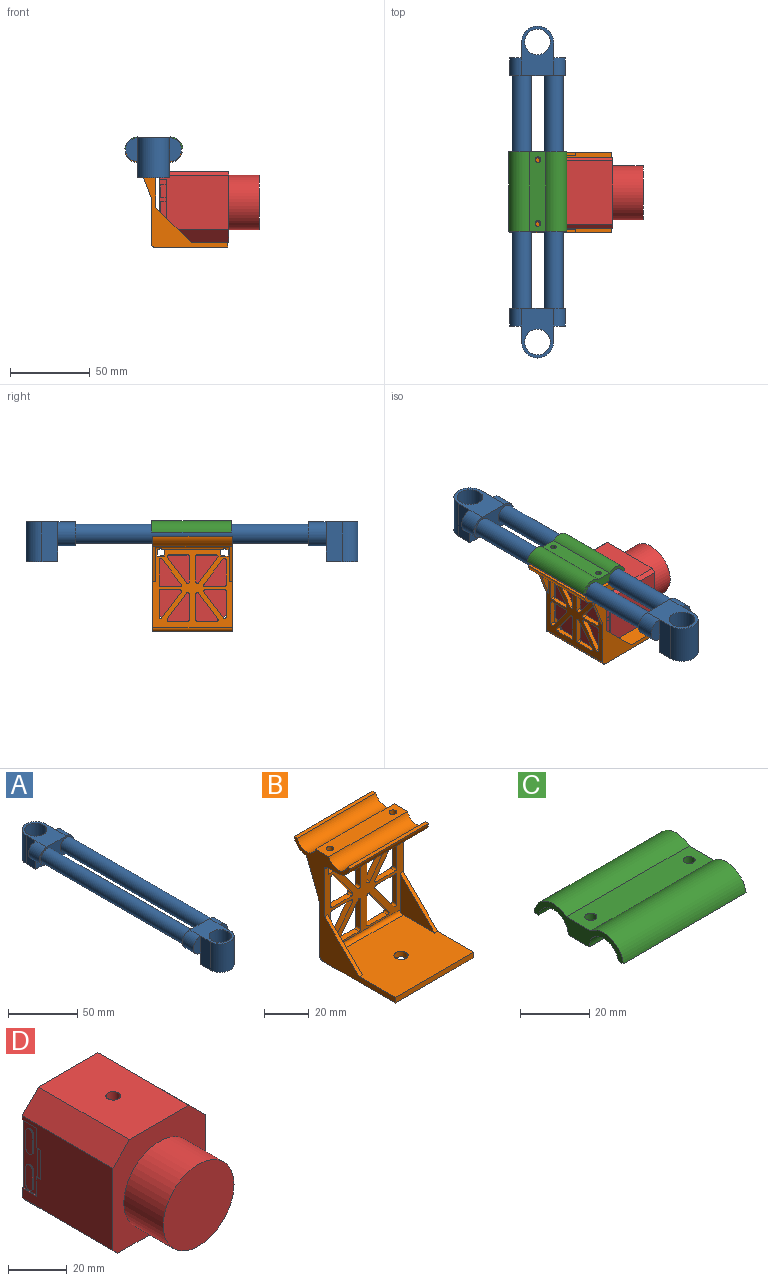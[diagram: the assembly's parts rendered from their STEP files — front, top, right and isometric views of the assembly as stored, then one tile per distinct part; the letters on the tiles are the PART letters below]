
ASSEMBLY  parts=4 mates=3
PART A: 28 faces, bbox 35x208x25 mm
  f0: plane 15x7.5mm, normal (0,1,0), area 88.4mm2, adj f11,f23
  f1: plane 15x7.5mm, normal (0,-1,0), area 88.4mm2, adj f7,f20
  f2: cylinder r=7.5mm len=15mm, axis (0,1,0), area 259.2mm2, adj f3,f4,f5,f6
  f3: plane 31x20mm, normal (0,0,1), area 376mm2, adj f2,f5,f7,f17,f18,f19,f20
  f4: plane 20x11mm, normal (0,0,-1), area 220mm2, adj f2,f5,f7,f16
  f5: plane 35x15mm, normal (0,1,0), area 250.5mm2, adj f2,f3,f4,f7,f8,f9
  f6: plane 15x7.5mm, normal (0,-1,0), area 88.4mm2, adj f2,f17
  f7: cylinder r=7.5mm len=15mm, axis (0,1,0), area 259.2mm2, adj f1,f3,f4,f5
  f8: cylinder r=6mm len=146mm, axis (0,1,0), area 5504.1mm2, adj f5,f10
  f9: cylinder r=6mm len=146mm, axis (0,1,0), area 5504.1mm2, adj f5,f10
  f10: plane 35x15mm, normal (0,-1,0), area 250.5mm2, adj f8,f9,f11,f12,f13,f14
  f11: cylinder r=7.5mm len=15mm, axis (0,-1,0), area 259.2mm2, adj f0,f10,f12,f13
  f12: plane 20x11mm, normal (0,0,-1), area 220mm2, adj f10,f11,f14,f22
  f13: plane 31x20mm, normal (0,0,1), area 376mm2, adj f10,f11,f14,f23,f24,f25,f26
  f14: cylinder r=7.5mm len=15mm, axis (0,-1,0), area 259.2mm2, adj f10,f12,f13,f15
  f15: plane 15x7.5mm, normal (0,1,0), area 88.4mm2, adj f14,f26
  f16: plane 20x10mm, normal (0,1,0), area 200mm2, adj f4,f17,f20,f21
  f17: plane 25x10mm, normal (-1,0,0), area 250mm2, adj f3,f6,f16,f18,f21
  f18: cylinder r=10mm len=25mm, axis (0,0,1), area 785.4mm2, adj f3,f17,f20,f21
  f19: cylinder r=8mm len=25mm, axis (0,0,1), area 1256.6mm2, adj f3,f21
  f20: plane 25x10mm, normal (1,0,0), area 250mm2, adj f1,f3,f16,f18,f21
  f21: plane 20x20mm, normal (0,0,-1), area 156mm2, adj f16,f17,f18,f19,f20
  f22: plane 20x10mm, normal (0,-1,0), area 200mm2, adj f12,f23,f26,f27
  f23: plane 25x10mm, normal (-1,0,0), area 250mm2, adj f0,f13,f22,f24,f27
  f24: cylinder r=10mm len=25mm, axis (0,0,1), area 785.4mm2, adj f13,f23,f26,f27
  f25: cylinder r=8mm len=25mm, axis (0,0,1), area 1256.6mm2, adj f13,f27
  f26: plane 25x10mm, normal (1,0,0), area 250mm2, adj f13,f15,f22,f24,f27
  f27: plane 20x20mm, normal (0,0,-1), area 156mm2, adj f22,f23,f24,f25,f26
PART B: 89 faces, bbox 50x64.4x59.5 mm
  f0: plane 50x46mm, normal (0,-1,0), area 1006.9mm2, adj f3,f6,f18,f19,f22,f23,f26,f27
  f1: plane 50x49mm, normal (0,1,0), area 1156.9mm2, adj f2,f13,f18,f19,f20,f21,f24,f25
  f2: cylinder r=2mm len=46mm, axis (-1,0,0), area 141.6mm2, adj f1,f7,f21,f25,f28,f29,f33,f34
  f3: cylinder r=2mm len=50mm, axis (-1,0,0), area 154.2mm2, adj f0,f10,f18,f19,f28,f29,f33,f34
  f4: plane 50x8.5mm, normal (0,0,1), area 405.8mm2, adj f16,f17,f18,f19,f28,f29
  f5: plane 50x43mm, normal (0,0,1), area 2038.3mm2, adj f6,f11,f18,f19,f22,f23,f26,f27
  f6: cylinder r=2mm len=46mm, axis (-1,0,0), area 144.5mm2, adj f0,f5,f23,f27
  f7: plane 46x6.5mm, normal (0,0,-1), area 299mm2, adj f2,f14,f21,f25
  f8: plane 50x2.05mm, normal (0,0,1), area 102.4mm2, adj f9,f17,f18,f19
  f9: cylinder r=8mm len=50mm, axis (-1,0,0), area 552.9mm2, adj f8,f10,f18,f19
  f10: plane 50x6.5mm, normal (0,0,-1), area 325mm2, adj f3,f9,f18,f19
  f11: plane 50x3mm, normal (0,-1,0), area 150mm2, adj f5,f12,f18,f19
  f12: plane 50x46mm, normal (0,0,-1), area 2268.3mm2, adj f11,f13,f18,f19,f40
  f13: cylinder r=2mm len=50mm, axis (-1,0,0), area 157.1mm2, adj f1,f12,f18,f19
  f14: cylinder r=8mm len=50mm, axis (-1,0,0), area 552.9mm2, adj f7,f15,f18,f19,f20,f24
  f15: plane 50x2.05mm, normal (0,0,1), area 102.4mm2, adj f14,f16,f18,f19
  f16: cylinder r=6mm len=50mm, axis (-1,0,0), area 779.8mm2, adj f4,f15,f18,f19
  f17: cylinder r=6mm len=50mm, axis (-1,0,0), area 779.8mm2, adj f4,f8,f18,f19
  f18: plane 64.36x59.5mm, normal (1,0,0), area 756.9mm2, adj f0,f1,f3,f4,f5,f8,f9,f10
  f19: plane 64.36x59.5mm, normal (-1,0,0), area 756.9mm2, adj f0,f1,f3,f4,f5,f8,f9,f10
  f20: plane 22x8.5mm, normal (0,0.93,-0.36), area 47.2mm2, adj f1,f14,f18,f21
  f21: plane 22x8.5mm, normal (-1,0,0), area 92.6mm2, adj f1,f2,f7,f20
  f22: plane 22x22mm, normal (0,-0.71,0.71), area 62.2mm2, adj f0,f5,f18,f23
  f23: plane 22x22mm, normal (-1,0,0), area 241.1mm2, adj f0,f5,f6,f22
  f24: plane 22x8.5mm, normal (0,0.93,-0.36), area 47.2mm2, adj f1,f14,f19,f25
  f25: plane 22x8.5mm, normal (1,0,0), area 92.6mm2, adj f1,f2,f7,f24
  f26: plane 22x22mm, normal (0,-0.71,0.71), area 62.2mm2, adj f0,f5,f19,f27
  f27: plane 22x22mm, normal (1,0,0), area 241.1mm2, adj f0,f5,f6,f26
  f28: cylinder r=1.75mm len=8.29mm, axis (0,0,1), area 88.2mm2, adj f2,f3,f4,f38,f39
  f29: cylinder r=1.75mm len=8.29mm, axis (0,0,1), area 88.2mm2, adj f2,f3,f4,f33,f34
  f30: plane 4.5x3mm, normal (0,0,1), area 13.5mm2, adj f0,f1,f31,f32
  f31: plane 4x3mm, normal (1,0,0), area 12mm2, adj f0,f1,f30,f33
  f32: plane 4x3mm, normal (-1,0,0), area 12mm2, adj f0,f1,f30,f34
  f33: plane 3x1.35mm, normal (0,0,-1), area 2.2mm2, adj f2,f3,f29,f31
  f34: plane 3x1.35mm, normal (0,0,-1), area 2.2mm2, adj f2,f3,f29,f32
  f35: plane 4.5x3mm, normal (0,0,1), area 13.5mm2, adj f0,f1,f36,f37
  f36: plane 4x3mm, normal (-1,0,0), area 12mm2, adj f0,f1,f35,f38
  f37: plane 4x3mm, normal (1,0,0), area 12mm2, adj f0,f1,f35,f39
  f38: plane 3x1.35mm, normal (0,0,-1), area 2.2mm2, adj f2,f3,f28,f36
  f39: plane 3x1.35mm, normal (0,0,-1), area 2.2mm2, adj f2,f3,f28,f37
  f40: cylinder r=3.17mm len=6.35mm, axis (0,0,-1), area 59.8mm2, adj f5,f12
  f41: plane 12x3mm, normal (0,0,-1), area 36mm2, adj f0,f1,f42,f46
  f42: cylinder r=1mm len=3mm, axis (0,1,0), area 4.7mm2, adj f0,f1,f41,f43
  f43: plane 16x3mm, normal (-1,0,0), area 48mm2, adj f0,f1,f42,f44
  f44: cylinder r=1mm len=3mm, axis (0,1,0), area 7.5mm2, adj f0,f1,f43,f45
  f45: plane 16x12mm, normal (0.8,0,0.6), area 60mm2, adj f0,f1,f44,f46
  f46: cylinder r=1mm len=3mm, axis (0,1,0), area 6.6mm2, adj f0,f1,f41,f45
  f47: cylinder r=1mm len=3mm, axis (0,1,0), area 7.5mm2, adj f0,f1,f48,f52
  f48: plane 16x3mm, normal (-1,0,0), area 48mm2, adj f0,f1,f47,f49
  f49: cylinder r=1mm len=3mm, axis (0,1,0), area 4.7mm2, adj f0,f1,f48,f50
  f50: plane 12x3mm, normal (0,0,1), area 36mm2, adj f0,f1,f49,f51
  f51: cylinder r=1mm len=3mm, axis (0,1,0), area 6.6mm2, adj f0,f1,f50,f52
  f52: plane 16x12mm, normal (0.8,0,-0.6), area 60mm2, adj f0,f1,f47,f51
  f53: cylinder r=1mm len=3mm, axis (0,1,0), area 6.6mm2, adj f0,f1,f54,f58
  f54: plane 12x3mm, normal (0,0,-1), area 36mm2, adj f0,f1,f53,f55
  f55: cylinder r=1mm len=3mm, axis (0,1,0), area 4.7mm2, adj f0,f1,f54,f56
  f56: plane 16x3mm, normal (-1,0,0), area 48mm2, adj f0,f1,f55,f57
  f57: cylinder r=1mm len=3mm, axis (0,1,0), area 7.5mm2, adj f0,f1,f56,f58
  f58: plane 16x12mm, normal (0.8,0,0.6), area 60mm2, adj f0,f1,f53,f57
  f59: plane 16x3mm, normal (1,0,0), area 48mm2, adj f0,f1,f60,f64
  f60: cylinder r=1mm len=3mm, axis (0,1,0), area 7.5mm2, adj f0,f1,f59,f61
  f61: plane 16x12mm, normal (-0.8,0,-0.6), area 60mm2, adj f0,f1,f60,f62
  f62: cylinder r=1mm len=3mm, axis (0,1,0), area 6.6mm2, adj f0,f1,f61,f63
  f63: plane 12x3mm, normal (0,0,1), area 36mm2, adj f0,f1,f62,f64
  f64: cylinder r=1mm len=3mm, axis (0,1,0), area 4.7mm2, adj f0,f1,f59,f63
  f65: cylinder r=1mm len=3mm, axis (0,1,0), area 7.5mm2, adj f0,f1,f66,f70
  f66: plane 16x12mm, normal (-0.8,0,-0.6), area 60mm2, adj f0,f1,f65,f67
  f67: cylinder r=1mm len=3mm, axis (0,1,0), area 6.6mm2, adj f0,f1,f66,f68
  f68: plane 12x3mm, normal (0,0,1), area 36mm2, adj f0,f1,f67,f69
  f69: cylinder r=1mm len=3mm, axis (0,1,0), area 4.7mm2, adj f0,f1,f68,f70
  f70: plane 16x3mm, normal (1,0,0), area 48mm2, adj f0,f1,f65,f69
  f71: cylinder r=1mm len=3mm, axis (0,1,0), area 7.5mm2, adj f0,f1,f72,f76
  f72: plane 16x3mm, normal (-1,0,0), area 48mm2, adj f0,f1,f71,f73
  f73: cylinder r=1mm len=3mm, axis (0,1,0), area 4.7mm2, adj f0,f1,f72,f74
  f74: plane 12x3mm, normal (0,0,1), area 36mm2, adj f0,f1,f73,f75
  f75: cylinder r=1mm len=3mm, axis (0,1,0), area 6.6mm2, adj f0,f1,f74,f76
  f76: plane 16x12mm, normal (0.8,0,-0.6), area 60mm2, adj f0,f1,f71,f75
  f77: cylinder r=1mm len=3mm, axis (0,1,0), area 6.6mm2, adj f0,f1,f78,f82
  f78: plane 16x12mm, normal (-0.8,0,0.6), area 60mm2, adj f0,f1,f77,f79
  f79: cylinder r=1mm len=3mm, axis (0,1,0), area 7.5mm2, adj f0,f1,f78,f80
  f80: plane 16x3mm, normal (1,0,0), area 48mm2, adj f0,f1,f79,f81
  f81: cylinder r=1mm len=3mm, axis (0,1,0), area 4.7mm2, adj f0,f1,f80,f82
  f82: plane 12x3mm, normal (0,0,-1), area 36mm2, adj f0,f1,f77,f81
  f83: plane 16x3mm, normal (1,0,0), area 48mm2, adj f0,f1,f84,f88
  f84: cylinder r=1mm len=3mm, axis (0,1,0), area 4.7mm2, adj f0,f1,f83,f85
  f85: plane 12x3mm, normal (0,0,-1), area 36mm2, adj f0,f1,f84,f86
  f86: cylinder r=1mm len=3mm, axis (0,1,0), area 6.6mm2, adj f0,f1,f85,f87
  f87: plane 16x12mm, normal (-0.8,0,0.6), area 60mm2, adj f0,f1,f86,f88
  f88: cylinder r=1mm len=3mm, axis (0,1,0), area 7.5mm2, adj f0,f1,f83,f87
PART C: 12 faces, bbox 50x36.3x8 mm
  f0: plane 50x9.98mm, normal (0,0,1), area 479.8mm2, adj f4,f5,f8,f9,f10,f11
  f1: plane 50x8.5mm, normal (0,0,-1), area 405.8mm2, adj f2,f7,f8,f9,f10,f11
  f2: cylinder r=6mm len=50mm, axis (-1,0,0), area 892.2mm2, adj f1,f3,f8,f9
  f3: plane 50x2mm, normal (0,0,-1), area 100mm2, adj f2,f4,f8,f9
  f4: cylinder r=7.98mm len=50mm, axis (-1,0,0), area 863.7mm2, adj f0,f3,f8,f9
  f5: cylinder r=7.98mm len=50mm, axis (-1,0,0), area 863.7mm2, adj f0,f6,f8,f9
  f6: plane 50x2mm, normal (0,0,-1), area 100mm2, adj f5,f7,f8,f9
  f7: cylinder r=6mm len=50mm, axis (-1,0,0), area 892.2mm2, adj f1,f6,f8,f9
  f8: plane 36.33x7.98mm, normal (1,0,0), area 120.2mm2, adj f0,f1,f2,f3,f4,f5,f6,f7
  f9: plane 36.33x7.98mm, normal (-1,0,0), area 120.2mm2, adj f0,f1,f2,f3,f4,f5,f6,f7
  f10: cylinder r=1.75mm len=6mm, axis (0,0,1), area 66mm2, adj f0,f1
  f11: cylinder r=1.75mm len=6mm, axis (0,0,1), area 66mm2, adj f0,f1
PART D: 49 faces, bbox 44.5x62.6x44.5 mm
  f0: plane 43.69x28.55mm, normal (0,0,1), area 1227.7mm2, adj f1,f2,f3,f4,f5
  f1: plane 43.69x7.95mm, normal (-0.71,0,0.71), area 491.2mm2, adj f0,f2,f3,f6
  f2: plane 44.45x44.45mm, normal (0,-1,0), area 999.2mm2, adj f0,f1,f4,f6,f7,f8,f9,f10
  f3: plane 44.45x44.45mm, normal (0,1,0), area 1878.8mm2, adj f0,f1,f4,f6,f7,f8,f9,f10
  f4: plane 43.69x7.95mm, normal (0.71,0,0.71), area 491.2mm2, adj f0,f2,f3,f7
  f5: cylinder r=2.5mm len=6mm, axis (0,0,1), area 94.2mm2, adj f0,f18
  f6: plane 43.69x34.17mm, normal (-1,0,0), area 1271.1mm2, adj f1,f2,f3,f10,f15,f17,f19,f20
  f7: plane 43.69x34.17mm, normal (1,0,0), area 1365.9mm2, adj f2,f3,f4,f8,f12,f14,f24
  f8: plane 43.69x2.33mm, normal (0.71,0,-0.71), area 144.2mm2, adj f2,f3,f7,f9
  f9: plane 43.69x39.78mm, normal (0,0,-1), area 1738.1mm2, adj f2,f3,f8,f10
  f10: plane 43.69x2.33mm, normal (-0.71,0,-0.71), area 144.2mm2, adj f2,f3,f6,f9
  f11: cylinder r=17mm len=34mm, axis (0,1,0), area 2020.9mm2, adj f2,f25
  f12: plane 4.45x0.5mm, normal (0,0,-1), area 2.2mm2, adj f3,f7,f13,f24
  f13: plane 28.5x4.45mm, normal (1,0,0), area 53.7mm2, adj f3,f12,f14,f24,f26,f27,f28,f29
  f14: plane 4.45x0.5mm, normal (0,0,1), area 2.2mm2, adj f3,f7,f13,f24
  f15: plane 6.9x0.5mm, normal (0,0,1), area 3.5mm2, adj f3,f6,f16,f19
  f16: plane 28.3x9.05mm, normal (-1,0,0), area 142.7mm2, adj f3,f15,f17,f19,f20,f21,f22,f23
  f17: plane 6.9x0.5mm, normal (0,0,-1), area 3.5mm2, adj f3,f6,f16,f23
  f18: plane 5x5mm, normal (0,0,1), area 19.6mm2, adj f5
  f19: plane 8.02x0.5mm, normal (0,1,0), area 4mm2, adj f6,f15,f16,f20
  f20: plane 2.15x0.5mm, normal (0,0,1), area 1.1mm2, adj f6,f16,f19,f21
  f21: plane 12.26x0.5mm, normal (0,1,0), area 6.1mm2, adj f6,f16,f20,f22
  f22: plane 2.15x0.5mm, normal (0,0,-1), area 1.1mm2, adj f6,f16,f21,f23
  f23: plane 8.02x0.5mm, normal (0,1,0), area 4mm2, adj f6,f16,f17,f22
  f24: plane 28.5x1mm, normal (0,1,0), area 24mm2, adj f7,f12,f13,f14,f26,f28,f29,f31
  f25: plane 34x34mm, normal (0,-1,0), area 907.9mm2, adj f11
  f26: plane 3.75x0.5mm, normal (0,0,1), area 1.9mm2, adj f13,f24,f27,f44
  f27: plane 8x0.5mm, normal (0,-1,0), area 4mm2, adj f13,f26,f28,f44
  f28: plane 3.75x0.5mm, normal (0,0,-1), area 1.9mm2, adj f13,f24,f27,f44
  f29: plane 3.75x0.5mm, normal (0,0,1), area 1.9mm2, adj f13,f24,f30,f45
  f30: plane 11.5x0.5mm, normal (0,-1,0), area 5.8mm2, adj f13,f29,f31,f45
  f31: plane 3.75x0.5mm, normal (0,0,-1), area 1.9mm2, adj f13,f24,f30,f45
  f32: cylinder r=1.6mm len=3.2mm, axis (1,0,0), area 2.5mm2, adj f16,f33,f35,f46
  f33: plane 7.2x0.5mm, normal (0,1,0), area 3.6mm2, adj f16,f32,f34,f46
  f34: cylinder r=1.6mm len=3.2mm, axis (1,0,0), area 2.5mm2, adj f16,f33,f35,f46
  f35: plane 7.2x0.5mm, normal (0,-1,0), area 3.6mm2, adj f16,f32,f34,f46
  f36: plane 11.72x0.5mm, normal (0,-1,0), area 5.9mm2, adj f16,f37,f39,f47
  f37: plane 1.43x0.5mm, normal (0,0,1), area 0.7mm2, adj f16,f36,f38,f47
  f38: plane 11.72x0.5mm, normal (0,1,0), area 5.9mm2, adj f16,f37,f39,f47
  f39: plane 1.43x0.5mm, normal (0,0,-1), area 0.7mm2, adj f16,f36,f38,f47
  f40: cylinder r=1.6mm len=3.2mm, axis (1,0,0), area 2.5mm2, adj f16,f41,f43,f48
  f41: plane 7.2x0.5mm, normal (0,1,0), area 3.6mm2, adj f16,f40,f42,f48
  f42: cylinder r=1.6mm len=3.2mm, axis (1,0,0), area 2.5mm2, adj f16,f41,f43,f48
  f43: plane 7.2x0.5mm, normal (0,-1,0), area 3.6mm2, adj f16,f40,f42,f48
  f44: plane 8x3.75mm, normal (1,0,0), area 30mm2, adj f24,f26,f27,f28
  f45: plane 11.5x3.75mm, normal (1,0,0), area 43.1mm2, adj f24,f29,f30,f31
  f46: plane 10.4x3.2mm, normal (-1,0,0), area 31.1mm2, adj f32,f33,f34,f35
  f47: plane 11.72x1.43mm, normal (-1,0,0), area 16.8mm2, adj f36,f37,f38,f39
  f48: plane 10.4x3.2mm, normal (-1,0,0), area 31.1mm2, adj f40,f41,f42,f43
PLACE A t=(-34.59,-16.32,-5.9)mm
PLACE B rot(axis=(0,0,1),90deg) t=(-34.59,-16.66,-13.9)mm
PLACE C rot(axis=(0,0,-1),90deg) t=(-34.34,-16.06,-5.9)mm
PLACE D rot(axis=(0.71,-0.71,0),180deg) t=(-31.09,-16.66,-41.68)mm
MATE fastened D.f5 <-> B.f40  axis (0,0,-1) through (-9.48,-16.66,-63.9)mm
MATE slider C.f7 <-> A.f8  axis (0,1,0) through (-44.59,-16.06,-5.9)mm
MATE slider B.f9 <-> A.f9  axis (0,-1,0) through (-24.59,-16.66,-5.9)mm
